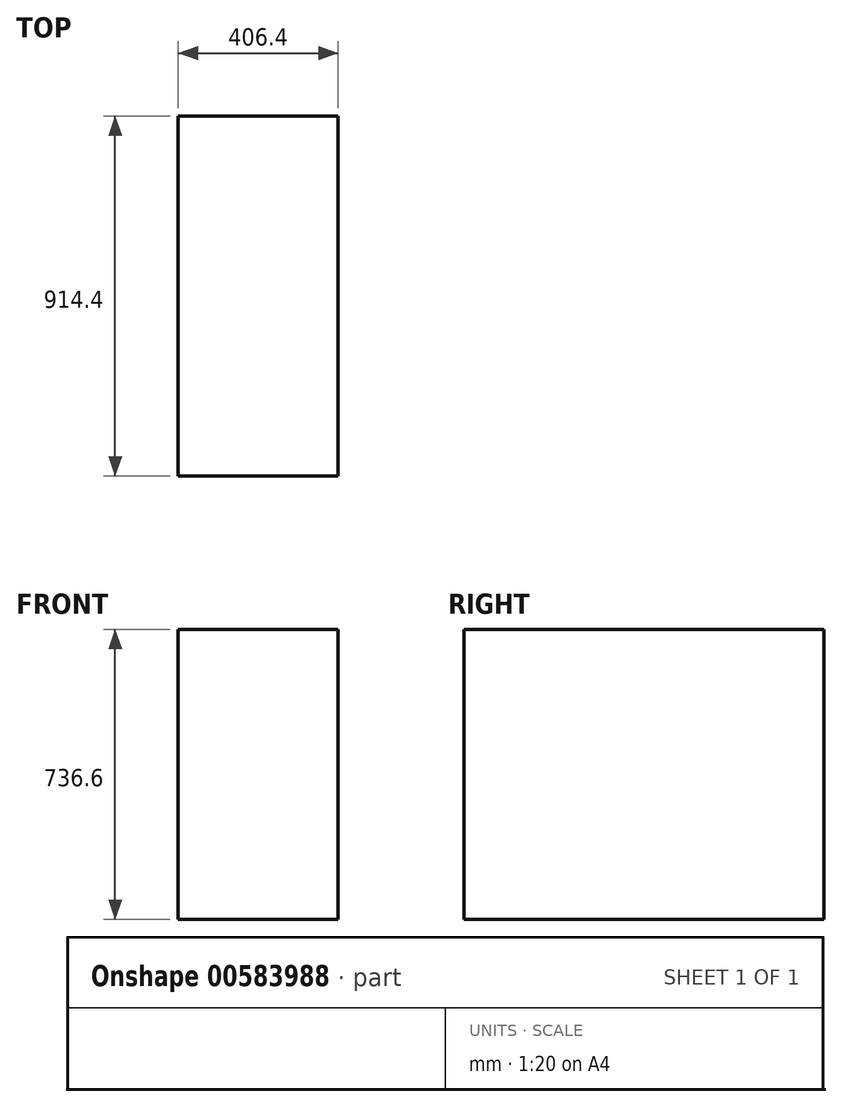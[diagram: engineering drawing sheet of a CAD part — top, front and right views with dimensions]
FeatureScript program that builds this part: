
annotation { "Feature Type Name" : "Feature", "Feature Type Description" : "" }
export const myFeature = defineFeature(function(context is Context, id is Id, definition is map)
    precondition{}
    {
        {
            var Q0;
            Q0=qCreatedBy(makeId("Top.planeOp"),FACE);
            var sketch = newSketch(context, id + "F0", { "sketchPlane" : qUnion([Q0])});
            skLineSegment(sketch, "E0.bottom", {"start": v(-197.36, 772.97) * mm, "end": v(209.04, 772.97) * mm});
            skLineSegment(sketch, "E0.top", {"start": v(-197.36, -141.43) * mm, "end": v(209.04, -141.43) * mm});
            skLineSegment(sketch, "E0.left", {"start": v(-197.36, 772.97) * mm, "end": v(-197.36, -141.43) * mm});
            skLineSegment(sketch, "E0.right", {"start": v(209.04, 772.97) * mm, "end": v(209.04, -141.43) * mm});
            skSolve(sketch);
        }
        {
            var Q0;
            Q0=makeQuery(id+"F0.imprint","IMPRINT",FACE,{"disambiguationData":[TD([[makeQuery(id+"F0.imprint","IMPRINT",EDGE,{"derivedFrom":sQuery(id+"F0.wireOp",EDGE,"E0.bottom")}),-1.0]])]});
            extrude(context, id + "F1", {"entities" : qUnion([Q0]), "depth" : 736.6 * mm, "offsetDistance" : 25.4 * mm});
        }
    });
